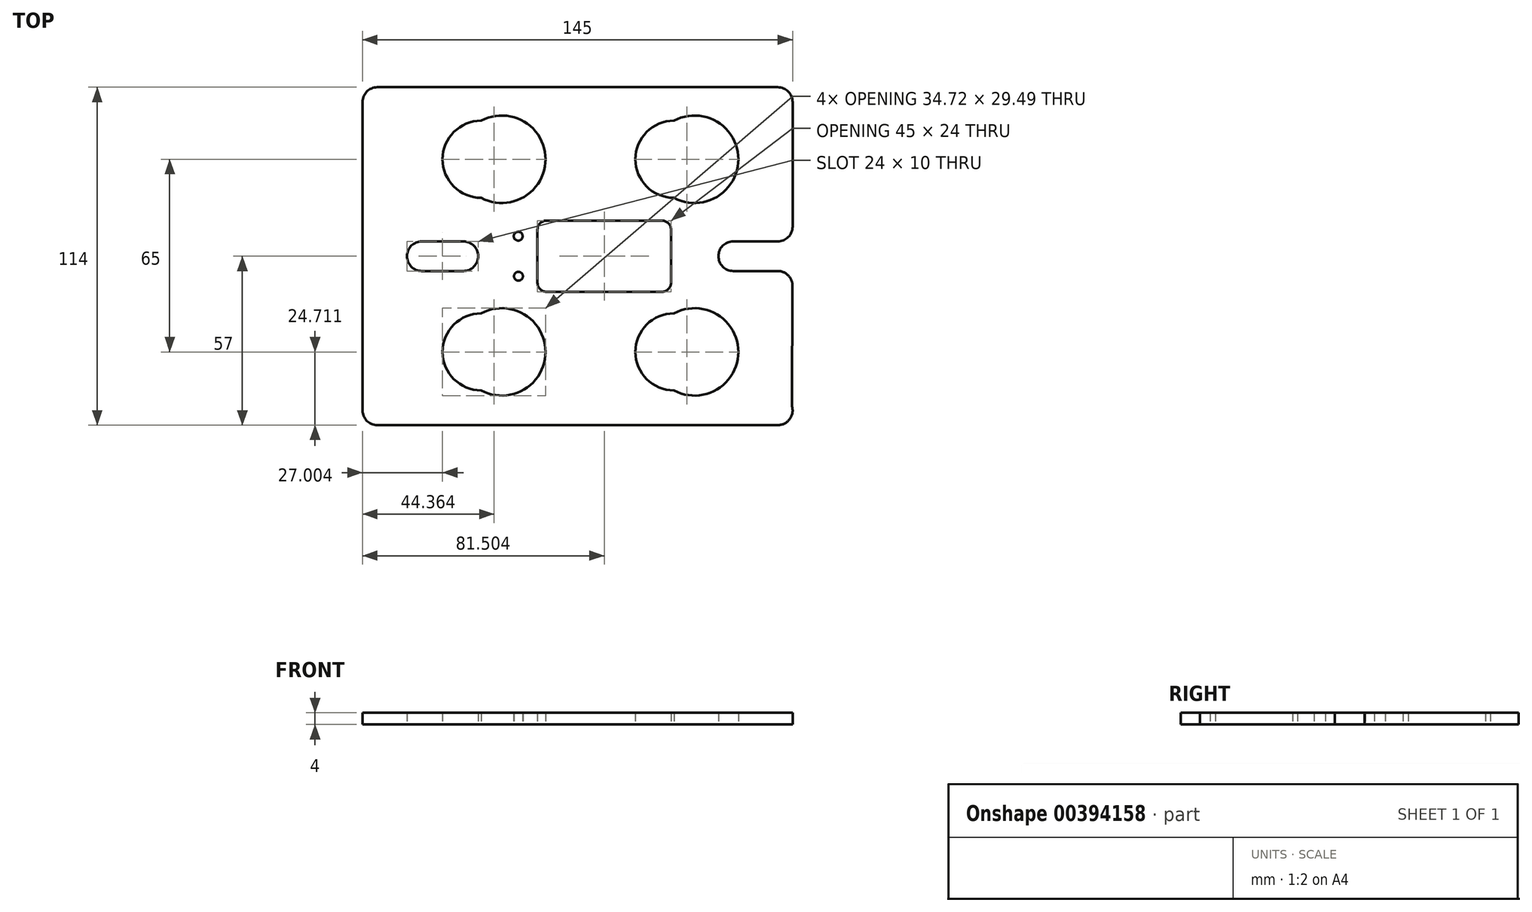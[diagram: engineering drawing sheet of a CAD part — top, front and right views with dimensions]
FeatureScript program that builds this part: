
annotation { "Feature Type Name" : "Feature", "Feature Type Description" : "" }
export const myFeature = defineFeature(function(context is Context, id is Id, definition is map)
    precondition{}
    {
        {
            var Q0;
            Q0=qCreatedBy(makeId("Top.planeOp"),FACE);
            var sketch = newSketch(context, id + "F0", { "sketchPlane" : qUnion([Q0])});
            skLineSegment(sketch, "E0.bottom", {"start": v(-97.07, 56.56) * mm, "end": v(37.93, 56.56) * mm});
            skLineSegment(sketch, "E0.top", {"start": v(-97.07, -57.44) * mm, "end": v(37.93, -57.44) * mm});
            skLineSegment(sketch, "E0.left", {"start": v(-102.07, 51.56) * mm, "end": v(-102.07, 16.56) * mm});
            skLineSegment(sketch, "E0.right", {"start": v(42.93, 51.56) * mm, "end": v(42.93, 9.56) * mm});
            skArc(sketch, "E1", {"start": v(-62.07, 45.27) * mm, "mid": v(-75.07, 32.27) * mm, "end": v(-62.07, 19.27) * mm});
            skArc(sketch, "E2", {"start": v(-62.07, 19.27) * mm, "mid": v(-40.35, 32.27) * mm, "end": v(-62.07, 45.27) * mm});
            skArc(sketch, "E3.0.1.0", {"start": v(-62.07, -19.73) * mm, "mid": v(-75.07, -32.73) * mm, "end": v(-62.07, -45.73) * mm});
            skArc(sketch, "E3.0.1.1", {"start": v(-62.07, -45.73) * mm, "mid": v(-40.35, -32.73) * mm, "end": v(-62.07, -19.73) * mm});
            skArc(sketch, "E3.1.0.0", {"start": v(2.93, 45.27) * mm, "mid": v(-10.07, 32.27) * mm, "end": v(2.93, 19.27) * mm});
            skArc(sketch, "E3.1.0.1", {"start": v(2.93, 19.27) * mm, "mid": v(24.65, 32.27) * mm, "end": v(2.93, 45.27) * mm});
            skArc(sketch, "E3.1.1.0", {"start": v(2.93, -19.73) * mm, "mid": v(-10.07, -32.73) * mm, "end": v(2.93, -45.73) * mm});
            skArc(sketch, "E3.1.1.1", {"start": v(2.93, -45.73) * mm, "mid": v(24.65, -32.73) * mm, "end": v(2.93, -19.73) * mm});
            skLineSegment(sketch, "E3.direction1", {"start": v(-62.07, 19.27) * mm, "end": v(2.93, 19.27) * mm, "construction": true});
            skLineSegment(sketch, "E3.direction2", {"start": v(-62.07, 19.27) * mm, "end": v(-62.07, -45.73) * mm, "construction": true});
            skPoint(sketch, "E4.visualSharp", {"position": v(-102.07, 56.56) * mm});
            skArc(sketch, "E4.filletArc", {"start": v(-97.07, 56.56) * mm, "mid": v(-100.6, 55.1) * mm, "end": v(-102.07, 51.56) * mm});
            skPoint(sketch, "E5.visualSharp", {"position": v(42.93, 56.56) * mm});
            skArc(sketch, "E5.filletArc", {"start": v(42.93, 51.56) * mm, "mid": v(41.47, 55.1) * mm, "end": v(37.93, 56.56) * mm});
            skPoint(sketch, "E6.visualSharp", {"position": v(42.93, -57.44) * mm});
            skArc(sketch, "E6.filletArc", {"start": v(37.93, -57.44) * mm, "mid": v(41.97, -55.4) * mm, "end": v(42.7, -50.94) * mm});
            skPoint(sketch, "E7.visualSharp", {"position": v(-102.07, -57.44) * mm});
            skArc(sketch, "E7.filletArc", {"start": v(-102.07, -52.44) * mm, "mid": v(-100.6, -55.98) * mm, "end": v(-97.07, -57.44) * mm});
            skLineSegment(sketch, "E8.trimOffspring", {"start": v(-102.07, -17.44) * mm, "end": v(-102.07, -52.44) * mm});
            skArc(sketch, "E9", {"start": v(-68.07, -5.44) * mm, "mid": v(-63.07, -0.44) * mm, "end": v(-68.07, 4.56) * mm});
            skArc(sketch, "E10", {"start": v(-82.07, 4.56) * mm, "mid": v(-87.07, -0.44) * mm, "end": v(-82.07, -5.44) * mm});
            skLineSegment(sketch, "E11", {"start": v(-82.07, 4.56) * mm, "end": v(-68.07, 4.56) * mm});
            skLineSegment(sketch, "E12", {"start": v(-82.07, -5.44) * mm, "end": v(-68.07, -5.44) * mm});
            skArc(sketch, "E13", {"start": v(22.93, 4.56) * mm, "mid": v(17.93, -0.44) * mm, "end": v(22.93, -5.44) * mm});
            skLineSegment(sketch, "E14", {"start": v(22.93, 4.56) * mm, "end": v(36.93, 4.56) * mm});
            skLineSegment(sketch, "E15", {"start": v(22.93, -5.44) * mm, "end": v(36.93, -5.44) * mm});
            skLineSegment(sketch, "E16", {"start": v(-102.07, 16.56) * mm, "end": v(-102.07, -17.44) * mm});
            skLineSegment(sketch, "E17", {"start": v(36.93, 4.56) * mm, "end": v(37.93, 4.56) * mm});
            skLineSegment(sketch, "E18", {"start": v(36.93, -5.44) * mm, "end": v(37.9, -5.44) * mm});
            skPoint(sketch, "E19.newPointA", {"position": v(42.93, 4.56) * mm});
            skArc(sketch, "E19.filletArc", {"start": v(37.93, 4.56) * mm, "mid": v(41.47, 6.02) * mm, "end": v(42.93, 9.56) * mm});
            skLineSegment(sketch, "E20", {"start": v(42.9, -10.47) * mm, "end": v(42.7, -50.94) * mm});
            skPoint(sketch, "E21.visualSharp", {"position": v(42.93, -5.44) * mm});
            skArc(sketch, "E21.filletArc", {"start": v(42.9, -10.47) * mm, "mid": v(41.45, -6.91) * mm, "end": v(37.9, -5.44) * mm});
            skLineSegment(sketch, "E22.bottom", {"start": v(-40.07, 11.56) * mm, "end": v(-1.07, 11.56) * mm});
            skLineSegment(sketch, "E22.top", {"start": v(-40.07, -12.44) * mm, "end": v(-1.07, -12.44) * mm});
            skLineSegment(sketch, "E22.left", {"start": v(-43.07, 8.56) * mm, "end": v(-43.07, -9.44) * mm});
            skLineSegment(sketch, "E22.right", {"start": v(1.93, 8.56) * mm, "end": v(1.93, -9.44) * mm});
            skPoint(sketch, "E23.visualSharp", {"position": v(1.93, -12.44) * mm});
            skArc(sketch, "E23.filletArc", {"start": v(-1.07, -12.44) * mm, "mid": v(1.06, -11.56) * mm, "end": v(1.93, -9.44) * mm});
            skPoint(sketch, "E24.visualSharp", {"position": v(1.93, 11.56) * mm});
            skArc(sketch, "E24.filletArc", {"start": v(1.93, 8.56) * mm, "mid": v(1.06, 10.68) * mm, "end": v(-1.07, 11.56) * mm});
            skPoint(sketch, "E25.visualSharp", {"position": v(-43.07, 11.56) * mm});
            skArc(sketch, "E25.filletArc", {"start": v(-40.07, 11.56) * mm, "mid": v(-42.19, 10.68) * mm, "end": v(-43.07, 8.56) * mm});
            skPoint(sketch, "E26.visualSharp", {"position": v(-43.07, -12.44) * mm});
            skArc(sketch, "E26.filletArc", {"start": v(-43.07, -9.44) * mm, "mid": v(-42.19, -11.56) * mm, "end": v(-40.07, -12.44) * mm});
            skCircle(sketch, "E27", {"center": v(-49.57, 6.3) * mm, "radius": 1.5 * mm});
            skCircle(sketch, "E28.1.0.0", {"center": v(-49.48, -7.19) * mm, "radius": 1.5 * mm});
            skLineSegment(sketch, "E28.direction1", {"start": v(-49.57, 6.3) * mm, "end": v(-49.48, -7.19) * mm, "construction": true});
            skSolve(sketch);
        }
        {
            var Q0;
            Q0=makeQuery(id+"F0.imprint","IMPRINT",FACE,{"disambiguationData":[TD([[makeQuery(id+"F0.imprint","IMPRINT",EDGE,{"derivedFrom":sQuery(id+"F0.wireOp",EDGE,"E0.bottom")}),-1.0]])]});
            extrude(context, id + "F1", {"entities" : qUnion([Q0]), "depth" : 4 * mm});
        }
    });
